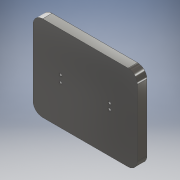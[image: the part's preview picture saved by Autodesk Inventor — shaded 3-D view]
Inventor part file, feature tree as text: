
AUTODESK INVENTOR PART (.ipt)
format: ipt  version: 2017 (Build 210142000, 142)  size: 161,792 bytes
history: native  units: mm
features: extrude x3, sketch x3, fillet x2, projected_geometry x2
ambient origin geometry x8: Origin, YZ Plane, XZ Plane, XY Plane, X Axis, Y Axis, Z Axis, Center Point
bodies: Solid1 (feature_tree)
feature tree (10):
  extrude  "Extrusion1"  Depth=20.0mm TaperAngle=0.0deg
  extrude  "Extrusion2"  Depth=71.0mm
  fillet  "Fillet1"  Radius=10.0mm
  fillet  "Fillet2"  Radius=20.0mm
  extrude  "Extrusion4"  Depth=12.0mm
  sketch  "Sketch2"  dims[d0=220.0mm d1=180.0mm d2=20.0mm d3=0.0mm]
  sketch  "Sketch3"  dims[d4=46.5mm d5=127.0mm d6=19.0mm d7=38.0mm d11=71.0mm d12=10.0mm d13=0.0mm d36=20.0mm]
  projected_geometry  "Projected Loop1"
  sketch  "Sketch5"  dims[d37=12.0mm d38=51.5mm d39=51.5mm d40=7.0mm d41=14.0mm d42=5.0mm d43=5.0mm d44=5.0mm d45=5.0mm d46=103.0mm d47=51.5mm d48=0.0mm d49=11.5mm d50=14.0mm d51=58.5mm d52=83.0mm d53=0.0mm d54=0.0mm]
  projected_geometry  "Projected Loop3"
